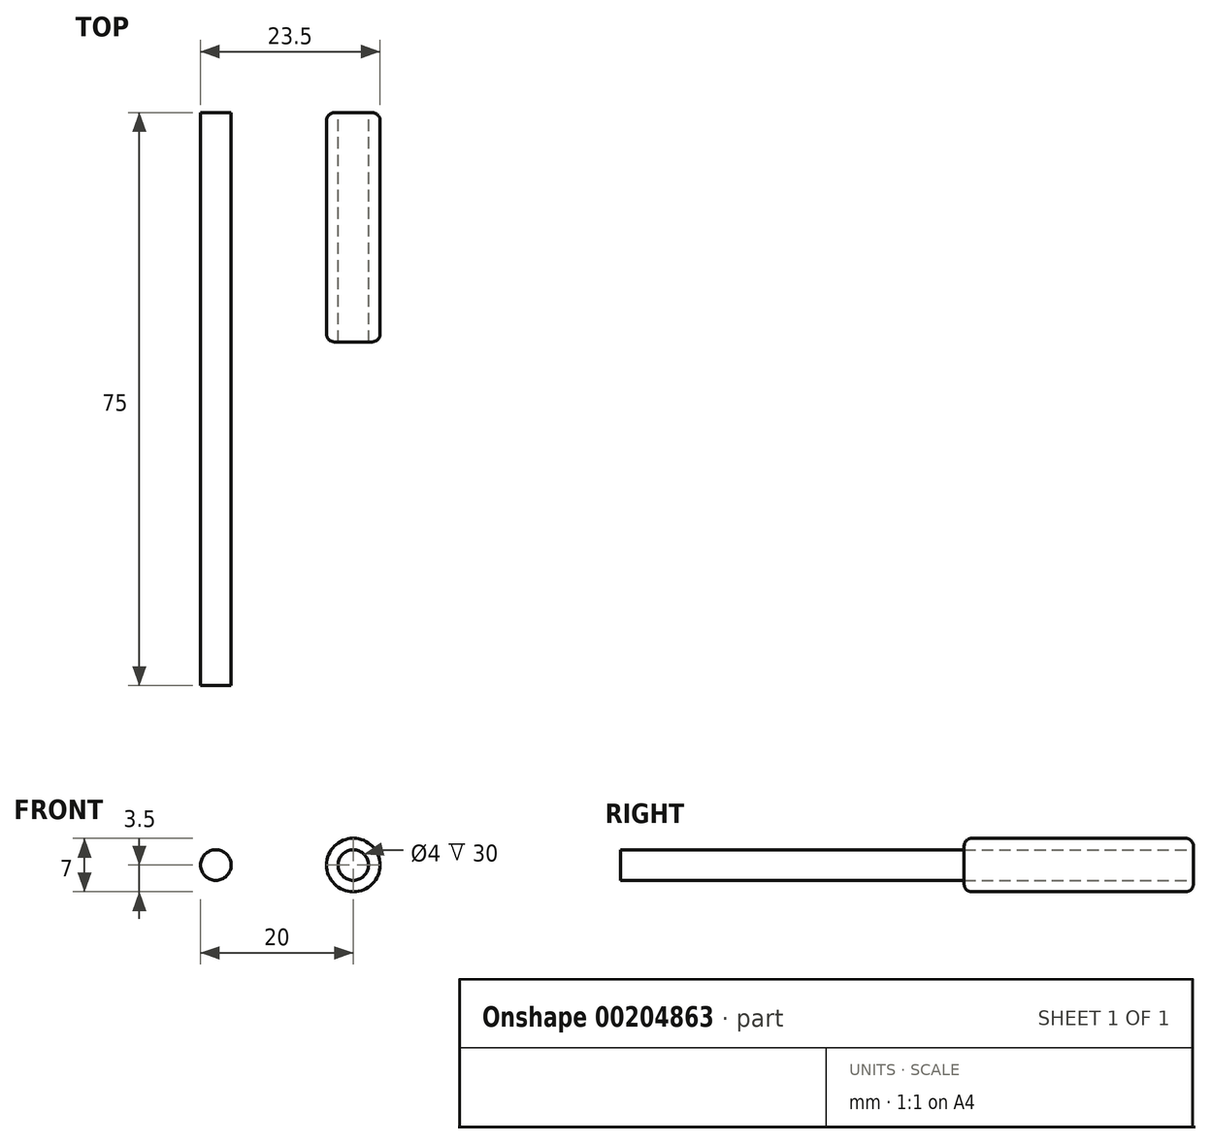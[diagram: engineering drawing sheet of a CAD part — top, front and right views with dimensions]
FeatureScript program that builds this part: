
annotation { "Feature Type Name" : "Feature", "Feature Type Description" : "" }
export const myFeature = defineFeature(function(context is Context, id is Id, definition is map)
    precondition{}
    {
        {
            var Q0;
            Q0=qCreatedBy(makeId("Front.planeOp"),FACE);
            var sketch = newSketch(context, id + "F0", { "sketchPlane" : qUnion([Q0])});
            skCircle(sketch, "E0", {"center": v(0, 0) * mm, "radius": 2 * mm});
            skCircle(sketch, "E1", {"center": v(0, 0) * mm, "radius": 3.5 * mm});
            skCircle(sketch, "E2", {"center": v(-18, 0) * mm, "radius": 2 * mm});
            skSolve(sketch);
        }
        {
            var Q0;
            Q0=makeQuery(id+"F0.imprint","IMPRINT",FACE,{"disambiguationData":[TD([[makeQuery(id+"F0.imprint","IMPRINT",EDGE,{"derivedFrom":sQuery(id+"F0.wireOp",EDGE,"E0")}),-1.0]])]});
            extrude(context, id + "F1", {"entities" : qUnion([Q0]), "depth" : 30 * mm});
        }
        {
            var Q0;
            Q0=makeQuery(id+"F1.opExtrude","CAP_EDGE",EDGE,{"disambiguationData":[OSD([sQuery(id+"F0.wireOp",EDGE,"E1")])],"isStart":false});
            var Q1;
            Q1=makeQuery(id+"F1.opExtrude","CAP_EDGE",EDGE,{"disambiguationData":[OSD([sQuery(id+"F0.wireOp",EDGE,"E1")])],"isStart":true});
            fillet(context, id + "F2", {"entities" : qUnion([Q0, Q1]), "radius" : 1 * mm, "tangentPropagation" : true, "allowEdgeOverflow" : false});
        }
        {
            var Q0;
            Q0=makeQuery(id+"F0.imprint","IMPRINT",FACE,{"disambiguationData":[TD([[makeQuery(id+"F0.imprint","IMPRINT",EDGE,{"derivedFrom":sQuery(id+"F0.wireOp",EDGE,"E2")}),1.0]])]});
            extrude(context, id + "F3", {"entities" : qUnion([Q0]), "depth" : 75 * mm});
        }
    });
